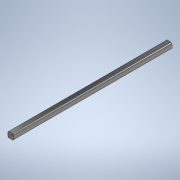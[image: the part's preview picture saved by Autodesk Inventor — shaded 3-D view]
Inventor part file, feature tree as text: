
AUTODESK INVENTOR PART (.ipt)
format: ipt  version: 2022.1 (Build 261234000, 234)  size: 120,832 bytes
history: native  units: mm
features: other x1, extrude x1, sketch x1
ambient origin geometry x8: Origin, YZ Plane, XZ Plane, XY Plane, X Axis, Y Axis, Z Axis, Center Point
bodies: Body1 (feature_tree)
feature tree (3):
  other  "Sólido1"
  extrude  "Extrusión1"  Depth=50.0mm
  sketch  "Boceto1"  dims[d0=50.0mm d1=50.0mm d2=10.0mm d3=10.0mm d4=10.0mm d5=10.0mm d6=4.0mm d7=1350.0mm d8=0.0mm]
